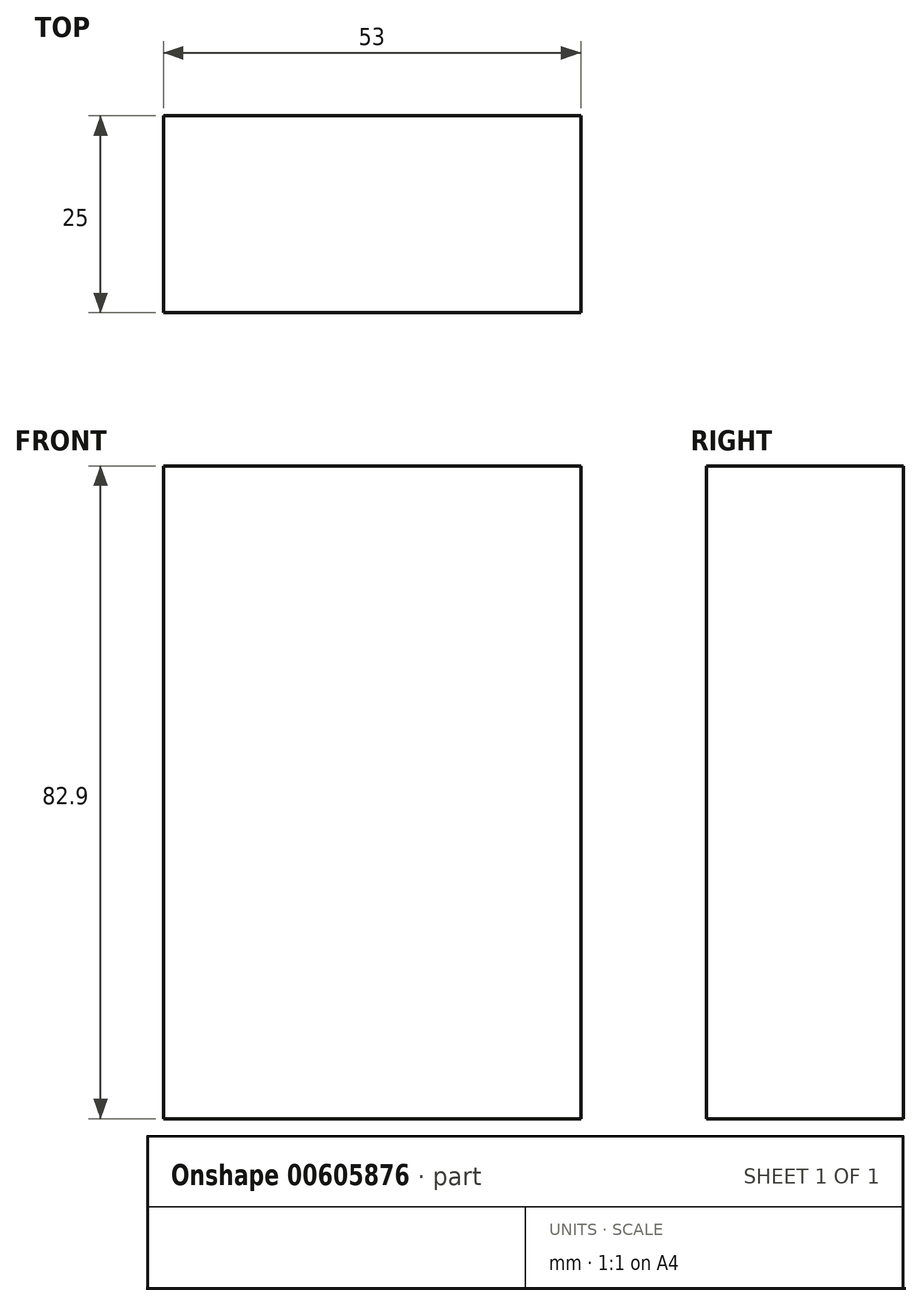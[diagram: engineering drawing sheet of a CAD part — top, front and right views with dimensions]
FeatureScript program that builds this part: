
annotation { "Feature Type Name" : "Feature", "Feature Type Description" : "" }
export const myFeature = defineFeature(function(context is Context, id is Id, definition is map)
    precondition{}
    {
        {
            var Q0;
            Q0=qCreatedBy(makeId("Front.planeOp"),FACE);
            var sketch = newSketch(context, id + "F0", { "sketchPlane" : qUnion([Q0])});
            skLineSegment(sketch, "E0", {"start": v(-44.75, 30.18) * mm, "end": v(8.25, 30.18) * mm});
            skLineSegment(sketch, "E1", {"start": v(-44.75, 30.18) * mm, "end": v(-44.75, -52.72) * mm});
            skLineSegment(sketch, "E2", {"start": v(8.25, 30.18) * mm, "end": v(8.25, -52.82) * mm});
            skLineSegment(sketch, "E3", {"start": v(-44.75, -52.72) * mm, "end": v(8.25, -52.72) * mm});
            skSolve(sketch);
        }
        {
            var Q0;
            Q0 = qSketchRegion(id + "F0", true);
            extrude(context, id + "F1", {"entities" : qUnion([Q0]), "depth" : 25 * mm, "offsetDistance" : 25 * mm});
        }
    });
